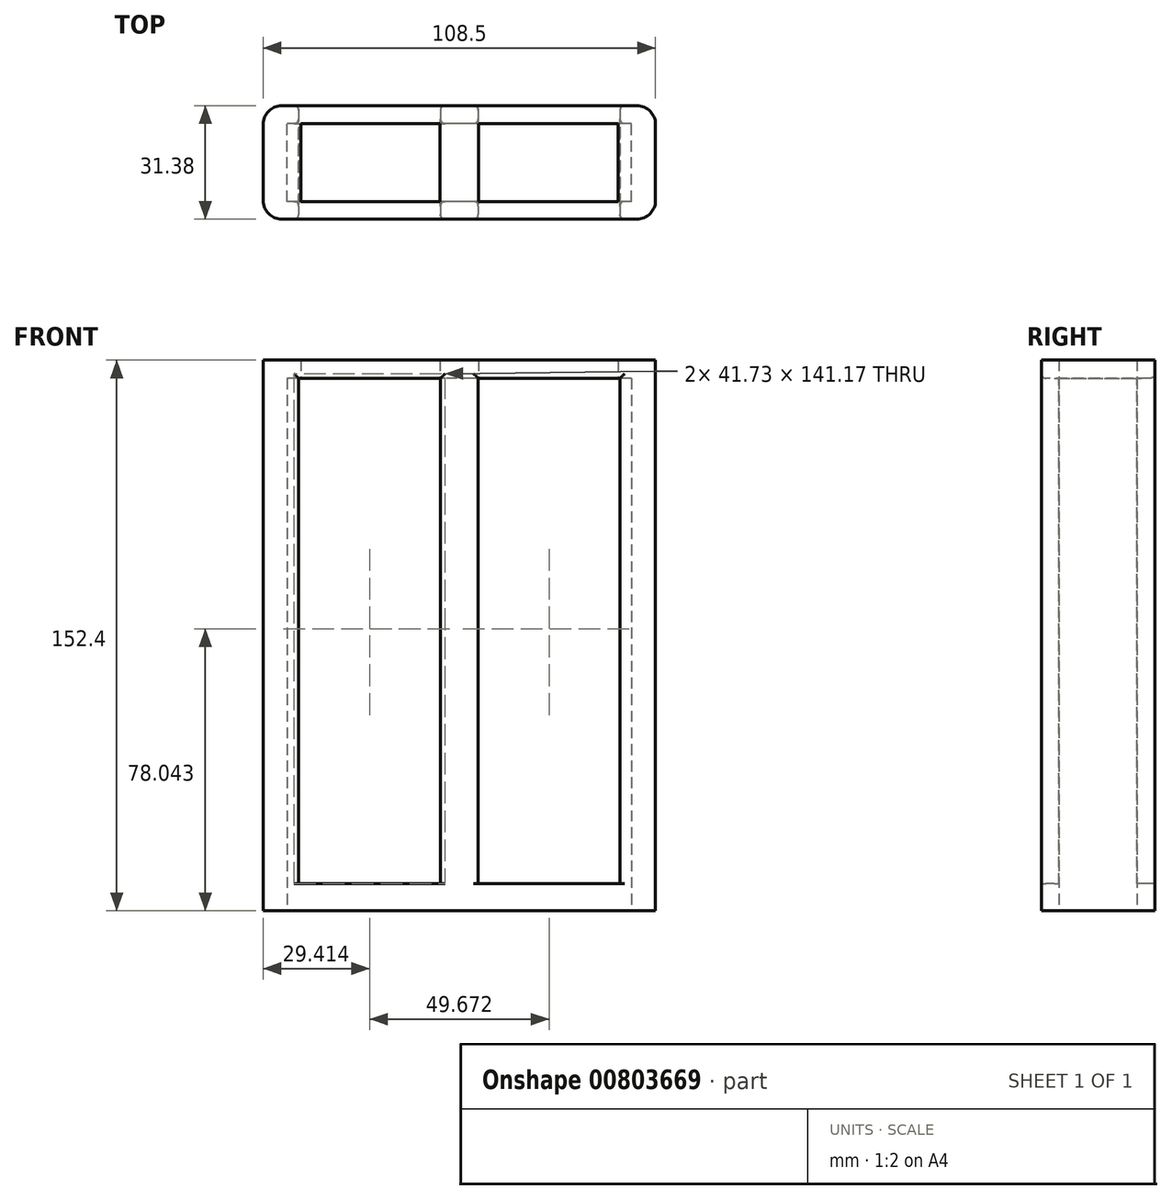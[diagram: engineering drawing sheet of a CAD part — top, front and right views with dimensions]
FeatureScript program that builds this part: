
annotation { "Feature Type Name" : "Feature", "Feature Type Description" : "" }
export const myFeature = defineFeature(function(context is Context, id is Id, definition is map)
    precondition{}
    {
        {
            var Q0;
            Q0=qCreatedBy(makeId("Top.planeOp"),FACE);
            var sketch = newSketch(context, id + "F0", { "sketchPlane" : qUnion([Q0])});
            skLineSegment(sketch, "E0.bottom", {"start": v(54.25, -15.69) * mm, "end": v(-54.25, -15.69) * mm});
            skLineSegment(sketch, "E0.top", {"start": v(54.25, 15.69) * mm, "end": v(-54.25, 15.69) * mm});
            skLineSegment(sketch, "E0.left", {"start": v(54.25, -15.69) * mm, "end": v(54.25, 15.69) * mm});
            skLineSegment(sketch, "E0.right", {"start": v(-54.25, -15.69) * mm, "end": v(-54.25, 15.69) * mm});
            skPoint(sketch, "E0.middle", {"position": v(0, 0) * mm});
            skSolve(sketch);
        }
        {
            var Q0;
            Q0 = qSketchRegion(id + "F0", true);
            extrude(context, id + "F1", {"entities" : qUnion([Q0]), "depth" : 152.4 * mm, "offsetDistance" : 25.4 * mm});
        }
        {
            var Q0;
            Q0=qCreatedBy(makeId("Top.planeOp"),FACE);
            var sketch = newSketch(context, id + "F2", { "sketchPlane" : qUnion([Q0])});
            skLineSegment(sketch, "E1.bottom", {"start": v(47.63, -10.8) * mm, "end": v(-47.63, -10.8) * mm});
            skLineSegment(sketch, "E1.top", {"start": v(47.63, 10.8) * mm, "end": v(-47.63, 10.8) * mm});
            skLineSegment(sketch, "E1.left", {"start": v(47.63, -10.8) * mm, "end": v(47.63, 10.8) * mm});
            skLineSegment(sketch, "E1.right", {"start": v(-47.63, -10.8) * mm, "end": v(-47.63, 10.8) * mm});
            skPoint(sketch, "E1.middle", {"position": v(0, 0) * mm});
            skSolve(sketch);
        }
        {
            var Q0;
            Q0 = qSketchRegion(id + "F2", true);
            extrude(context, id + "F3", {"entities" : qUnion([Q0]), "operationType" : NewBodyOperationType.REMOVE, "depth" : 147.32 * mm, "offsetDistance" : 25.4 * mm});
        }
        {
            var Q0;
            Q0=makeQuery(id+"F1.opExtrude","SWEPT_EDGE",EDGE,{"disambiguationData":[OSD([sQuery(id+"F0.wireOp",EDGE,"E0.top"),sQuery(id+"F0.wireOp",EDGE,"E0.right")])]});
            var Q1;
            Q1=makeQuery(id+"F1.opExtrude","SWEPT_EDGE",EDGE,{"disambiguationData":[OSD([sQuery(id+"F0.wireOp",EDGE,"E0.bottom"),sQuery(id+"F0.wireOp",EDGE,"E0.right")])]});
            var Q2;
            Q2=makeQuery(id+"F1.opExtrude","SWEPT_EDGE",EDGE,{"disambiguationData":[OSD([sQuery(id+"F0.wireOp",EDGE,"E0.bottom"),sQuery(id+"F0.wireOp",EDGE,"E0.left")])]});
            var Q3;
            Q3=makeQuery(id+"F1.opExtrude","SWEPT_EDGE",EDGE,{"disambiguationData":[OSD([sQuery(id+"F0.wireOp",EDGE,"E0.top"),sQuery(id+"F0.wireOp",EDGE,"E0.left")])]});
            fillet(context, id + "F4", {"entities" : qUnion([Q0, Q1, Q2, Q3]), "radius" : 5.08 * mm, "tangentPropagation" : true, "allowEdgeOverflow" : false});
        }
        {
            var Q0;
            Q0=qCreatedBy(makeId("Front.planeOp"),FACE);
            var sketch = newSketch(context, id + "F5", { "sketchPlane" : qUnion([Q0])});
            skLineSegment(sketch, "E2.bottom", {"start": v(44.43, 7.46) * mm, "end": v(5.24, 7.46) * mm});
            skLineSegment(sketch, "E2.top", {"start": v(44.43, 147.36) * mm, "end": v(5.24, 147.36) * mm});
            skLineSegment(sketch, "E2.left", {"start": v(44.43, 7.46) * mm, "end": v(44.43, 147.36) * mm});
            skLineSegment(sketch, "E2.right", {"start": v(5.24, 7.46) * mm, "end": v(5.24, 147.36) * mm});
            skLineSegment(sketch, "E3.MirrorCS", {"start": v(-5.24, 7.46) * mm, "end": v(-5.24, 147.36) * mm});
            skLineSegment(sketch, "E4.MirrorCS", {"start": v(-44.43, 7.46) * mm, "end": v(-5.24, 7.46) * mm});
            skLineSegment(sketch, "E5.MirrorCS", {"start": v(-44.43, 7.46) * mm, "end": v(-44.43, 147.36) * mm});
            skLineSegment(sketch, "E6.MirrorCS", {"start": v(-44.43, 147.36) * mm, "end": v(-5.24, 147.36) * mm});
            skSolve(sketch);
        }
        {
            var Q0;
            Q0 = qSketchRegion(id + "F5", true);
            extrude(context, id + "F6", {"entities" : qUnion([Q0]), "operationType" : NewBodyOperationType.REMOVE, "endBound" : BoundingType.THROUGH_ALL, "oppositeDirection" : true, "depth" : 25.4 * mm, "offsetDistance" : 25.4 * mm, "hasSecondDirection" : true, "secondDirectionBound" : SecondDirectionBoundingType.THROUGH_ALL, "secondDirectionOppositeDirection" : false, "secondDirectionDepth" : 25.4 * mm});
        }
        {
            var Q0;
            Q0=makeQuery(id+"F6.boolean.opBoolean","INTERSECT",EDGE,{"derivedFrom":[makeQuery(id+"F1.opExtrude","SWEPT_FACE",FACE,{"disambiguationData":[OSD([sQuery(id+"F0.wireOp",EDGE,"E0.bottom")])]}),makeQuery(id+"F6.opExtrude","SWEPT_FACE",FACE,{"disambiguationData":[OSD([sQuery(id+"F5.wireOp",EDGE,"E2.right")])]})]});
            var Q1;
            Q1=makeQuery(id+"F6.boolean.opBoolean","INTERSECT",EDGE,{"derivedFrom":[makeQuery(id+"F3.boolean.opBoolean","COPY",FACE,{"derivedFrom":makeQuery(id+"F3.opExtrude","SWEPT_FACE",FACE,{"disambiguationData":[OSD([sQuery(id+"F2.wireOp",EDGE,"E1.bottom")])]})}),makeQuery(id+"F6.opExtrude","SWEPT_FACE",FACE,{"disambiguationData":[OSD([sQuery(id+"F5.wireOp",EDGE,"E2.right")])]})]});
            var Q2;
            Q2=makeQuery(id+"F6.boolean.opBoolean","INTERSECT",EDGE,{"derivedFrom":[makeQuery(id+"F1.opExtrude","SWEPT_FACE",FACE,{"disambiguationData":[OSD([sQuery(id+"F0.wireOp",EDGE,"E0.bottom")])]}),makeQuery(id+"F6.opExtrude","SWEPT_FACE",FACE,{"disambiguationData":[OSD([sQuery(id+"F5.wireOp",EDGE,"E3.MirrorCS")])]})]});
            var Q3;
            Q3=makeQuery(id+"F6.boolean.opBoolean","INTERSECT",EDGE,{"derivedFrom":[makeQuery(id+"F3.boolean.opBoolean","COPY",FACE,{"derivedFrom":makeQuery(id+"F3.opExtrude","SWEPT_FACE",FACE,{"disambiguationData":[OSD([sQuery(id+"F2.wireOp",EDGE,"E1.bottom")])]})}),makeQuery(id+"F6.opExtrude","SWEPT_FACE",FACE,{"disambiguationData":[OSD([sQuery(id+"F5.wireOp",EDGE,"E3.MirrorCS")])]})]});
            var Q4;
            Q4=makeQuery(id+"F6.boolean.opBoolean","INTERSECT",EDGE,{"derivedFrom":[makeQuery(id+"F3.boolean.opBoolean","COPY",FACE,{"derivedFrom":makeQuery(id+"F3.opExtrude","SWEPT_FACE",FACE,{"disambiguationData":[OSD([sQuery(id+"F2.wireOp",EDGE,"E1.top")])]})}),makeQuery(id+"F6.opExtrude","SWEPT_FACE",FACE,{"disambiguationData":[OSD([sQuery(id+"F5.wireOp",EDGE,"E3.MirrorCS")])]})]});
            var Q5;
            Q5=makeQuery(id+"F6.boolean.opBoolean","INTERSECT",EDGE,{"derivedFrom":[makeQuery(id+"F1.opExtrude","SWEPT_FACE",FACE,{"disambiguationData":[OSD([sQuery(id+"F0.wireOp",EDGE,"E0.top")])]}),makeQuery(id+"F6.opExtrude","SWEPT_FACE",FACE,{"disambiguationData":[OSD([sQuery(id+"F5.wireOp",EDGE,"E3.MirrorCS")])]})]});
            var Q6;
            Q6=makeQuery(id+"F6.boolean.opBoolean","INTERSECT",EDGE,{"derivedFrom":[makeQuery(id+"F3.boolean.opBoolean","COPY",FACE,{"derivedFrom":makeQuery(id+"F3.opExtrude","SWEPT_FACE",FACE,{"disambiguationData":[OSD([sQuery(id+"F2.wireOp",EDGE,"E1.top")])]})}),makeQuery(id+"F6.opExtrude","SWEPT_FACE",FACE,{"disambiguationData":[OSD([sQuery(id+"F5.wireOp",EDGE,"E2.right")])]})]});
            var Q7;
            Q7=makeQuery(id+"F6.boolean.opBoolean","INTERSECT",EDGE,{"derivedFrom":[makeQuery(id+"F1.opExtrude","SWEPT_FACE",FACE,{"disambiguationData":[OSD([sQuery(id+"F0.wireOp",EDGE,"E0.top")])]}),makeQuery(id+"F6.opExtrude","SWEPT_FACE",FACE,{"disambiguationData":[OSD([sQuery(id+"F5.wireOp",EDGE,"E2.right")])]})]});
            var Q8;
            Q8=makeQuery(id+"F6.boolean.opBoolean","INTERSECT",EDGE,{"derivedFrom":[makeQuery(id+"F1.opExtrude","SWEPT_FACE",FACE,{"disambiguationData":[OSD([sQuery(id+"F0.wireOp",EDGE,"E0.bottom")])]}),makeQuery(id+"F6.opExtrude","SWEPT_FACE",FACE,{"disambiguationData":[OSD([sQuery(id+"F5.wireOp",EDGE,"E2.left")])]})]});
            var Q9;
            Q9=makeQuery(id+"F6.boolean.opBoolean","INTERSECT",EDGE,{"derivedFrom":[makeQuery(id+"F3.boolean.opBoolean","COPY",FACE,{"derivedFrom":makeQuery(id+"F3.opExtrude","SWEPT_FACE",FACE,{"disambiguationData":[OSD([sQuery(id+"F2.wireOp",EDGE,"E1.bottom")])]})}),makeQuery(id+"F6.opExtrude","SWEPT_FACE",FACE,{"disambiguationData":[OSD([sQuery(id+"F5.wireOp",EDGE,"E2.left")])]})]});
            var Q10;
            Q10=makeQuery(id+"F6.boolean.opBoolean","INTERSECT",EDGE,{"derivedFrom":[makeQuery(id+"F3.boolean.opBoolean","COPY",FACE,{"derivedFrom":makeQuery(id+"F3.opExtrude","SWEPT_FACE",FACE,{"disambiguationData":[OSD([sQuery(id+"F2.wireOp",EDGE,"E1.top")])]})}),makeQuery(id+"F6.opExtrude","SWEPT_FACE",FACE,{"disambiguationData":[OSD([sQuery(id+"F5.wireOp",EDGE,"E2.left")])]})]});
            var Q11;
            Q11=makeQuery(id+"F6.boolean.opBoolean","INTERSECT",EDGE,{"derivedFrom":[makeQuery(id+"F1.opExtrude","SWEPT_FACE",FACE,{"disambiguationData":[OSD([sQuery(id+"F0.wireOp",EDGE,"E0.top")])]}),makeQuery(id+"F6.opExtrude","SWEPT_FACE",FACE,{"disambiguationData":[OSD([sQuery(id+"F5.wireOp",EDGE,"E2.left")])]})]});
            var Q12;
            Q12=makeQuery(id+"F6.boolean.opBoolean","INTERSECT",EDGE,{"derivedFrom":[makeQuery(id+"F3.boolean.opBoolean","COPY",FACE,{"derivedFrom":makeQuery(id+"F3.opExtrude","SWEPT_FACE",FACE,{"disambiguationData":[OSD([sQuery(id+"F2.wireOp",EDGE,"E1.top")])]})}),makeQuery(id+"F6.opExtrude","SWEPT_FACE",FACE,{"disambiguationData":[OSD([sQuery(id+"F5.wireOp",EDGE,"E5.MirrorCS")])]})]});
            var Q13;
            Q13=makeQuery(id+"F6.boolean.opBoolean","INTERSECT",EDGE,{"derivedFrom":[makeQuery(id+"F1.opExtrude","SWEPT_FACE",FACE,{"disambiguationData":[OSD([sQuery(id+"F0.wireOp",EDGE,"E0.top")])]}),makeQuery(id+"F6.opExtrude","SWEPT_FACE",FACE,{"disambiguationData":[OSD([sQuery(id+"F5.wireOp",EDGE,"E5.MirrorCS")])]})]});
            var Q14;
            Q14=makeQuery(id+"F6.boolean.opBoolean","INTERSECT",EDGE,{"derivedFrom":[makeQuery(id+"F3.boolean.opBoolean","COPY",FACE,{"derivedFrom":makeQuery(id+"F3.opExtrude","SWEPT_FACE",FACE,{"disambiguationData":[OSD([sQuery(id+"F2.wireOp",EDGE,"E1.bottom")])]})}),makeQuery(id+"F6.opExtrude","SWEPT_FACE",FACE,{"disambiguationData":[OSD([sQuery(id+"F5.wireOp",EDGE,"E5.MirrorCS")])]})]});
            var Q15;
            Q15=makeQuery(id+"F6.boolean.opBoolean","INTERSECT",EDGE,{"derivedFrom":[makeQuery(id+"F1.opExtrude","SWEPT_FACE",FACE,{"disambiguationData":[OSD([sQuery(id+"F0.wireOp",EDGE,"E0.bottom")])]}),makeQuery(id+"F6.opExtrude","SWEPT_FACE",FACE,{"disambiguationData":[OSD([sQuery(id+"F5.wireOp",EDGE,"E5.MirrorCS")])]})]});
            var Q16;
            Q16=makeQuery(id+"F6.boolean.opBoolean","INTERSECT",EDGE,{"derivedFrom":[makeQuery(id+"F1.opExtrude","SWEPT_FACE",FACE,{"disambiguationData":[OSD([sQuery(id+"F0.wireOp",EDGE,"E0.top")])]}),makeQuery(id+"F6.opExtrude","SWEPT_FACE",FACE,{"disambiguationData":[OSD([sQuery(id+"F5.wireOp",EDGE,"E6.MirrorCS")])]})]});
            var Q17;
            Q17=makeQuery(id+"F6.boolean.opBoolean","INTERSECT",EDGE,{"derivedFrom":[makeQuery(id+"F1.opExtrude","SWEPT_FACE",FACE,{"disambiguationData":[OSD([sQuery(id+"F0.wireOp",EDGE,"E0.bottom")])]}),makeQuery(id+"F6.opExtrude","SWEPT_FACE",FACE,{"disambiguationData":[OSD([sQuery(id+"F5.wireOp",EDGE,"E6.MirrorCS")])]})]});
            var Q18;
            Q18=makeQuery(id+"F6.boolean.opBoolean","INTERSECT",EDGE,{"derivedFrom":[makeQuery(id+"F1.opExtrude","SWEPT_FACE",FACE,{"disambiguationData":[OSD([sQuery(id+"F0.wireOp",EDGE,"E0.bottom")])]}),makeQuery(id+"F6.opExtrude","SWEPT_FACE",FACE,{"disambiguationData":[OSD([sQuery(id+"F5.wireOp",EDGE,"E2.top")])]})]});
            var Q19;
            Q19=makeQuery(id+"F6.boolean.opBoolean","INTERSECT",EDGE,{"derivedFrom":[makeQuery(id+"F1.opExtrude","SWEPT_FACE",FACE,{"disambiguationData":[OSD([sQuery(id+"F0.wireOp",EDGE,"E0.top")])]}),makeQuery(id+"F6.opExtrude","SWEPT_FACE",FACE,{"disambiguationData":[OSD([sQuery(id+"F5.wireOp",EDGE,"E2.top")])]})]});
            fillet(context, id + "F7", {"entities" : qUnion([Q0, Q1, Q2, Q3, Q4, Q5, Q6, Q7, Q8, Q9, Q10, Q11, Q12, Q13, Q14, Q15, Q16, Q17, Q18, Q19]), "radius" : 1.27 * mm, "tangentPropagation" : true, "allowEdgeOverflow" : false});
        }
        {
            var Q0;
            Q0=qCreatedBy(makeId("Top.planeOp"),FACE);
            var sketch = newSketch(context, id + "F8", { "sketchPlane" : qUnion([Q0])});
            skLineSegment(sketch, "E7.bottom", {"start": v(-43.9, -10.8) * mm, "end": v(-5.32, -10.8) * mm});
            skLineSegment(sketch, "E7.top", {"start": v(-43.9, 10.8) * mm, "end": v(-5.32, 10.8) * mm});
            skLineSegment(sketch, "E7.left", {"start": v(-43.9, -10.8) * mm, "end": v(-43.9, 10.8) * mm});
            skLineSegment(sketch, "E7.right", {"start": v(-5.32, -10.8) * mm, "end": v(-5.32, 10.8) * mm});
            skLineSegment(sketch, "E8.MirrorCS", {"start": v(5.32, -10.8) * mm, "end": v(5.32, 10.8) * mm});
            skLineSegment(sketch, "E9.MirrorCS", {"start": v(43.9, -10.8) * mm, "end": v(5.32, -10.8) * mm});
            skLineSegment(sketch, "E10.MirrorCS", {"start": v(43.9, -10.8) * mm, "end": v(43.9, 10.8) * mm});
            skLineSegment(sketch, "E11.MirrorCS", {"start": v(43.9, 10.8) * mm, "end": v(5.32, 10.8) * mm});
            skSolve(sketch);
        }
        {
            var Q0;
            Q0 = qSketchRegion(id + "F8", true);
            extrude(context, id + "F9", {"entities" : qUnion([Q0]), "operationType" : NewBodyOperationType.REMOVE, "endBound" : BoundingType.THROUGH_ALL, "depth" : 25.4 * mm, "offsetDistance" : 25.4 * mm});
        }
    });
